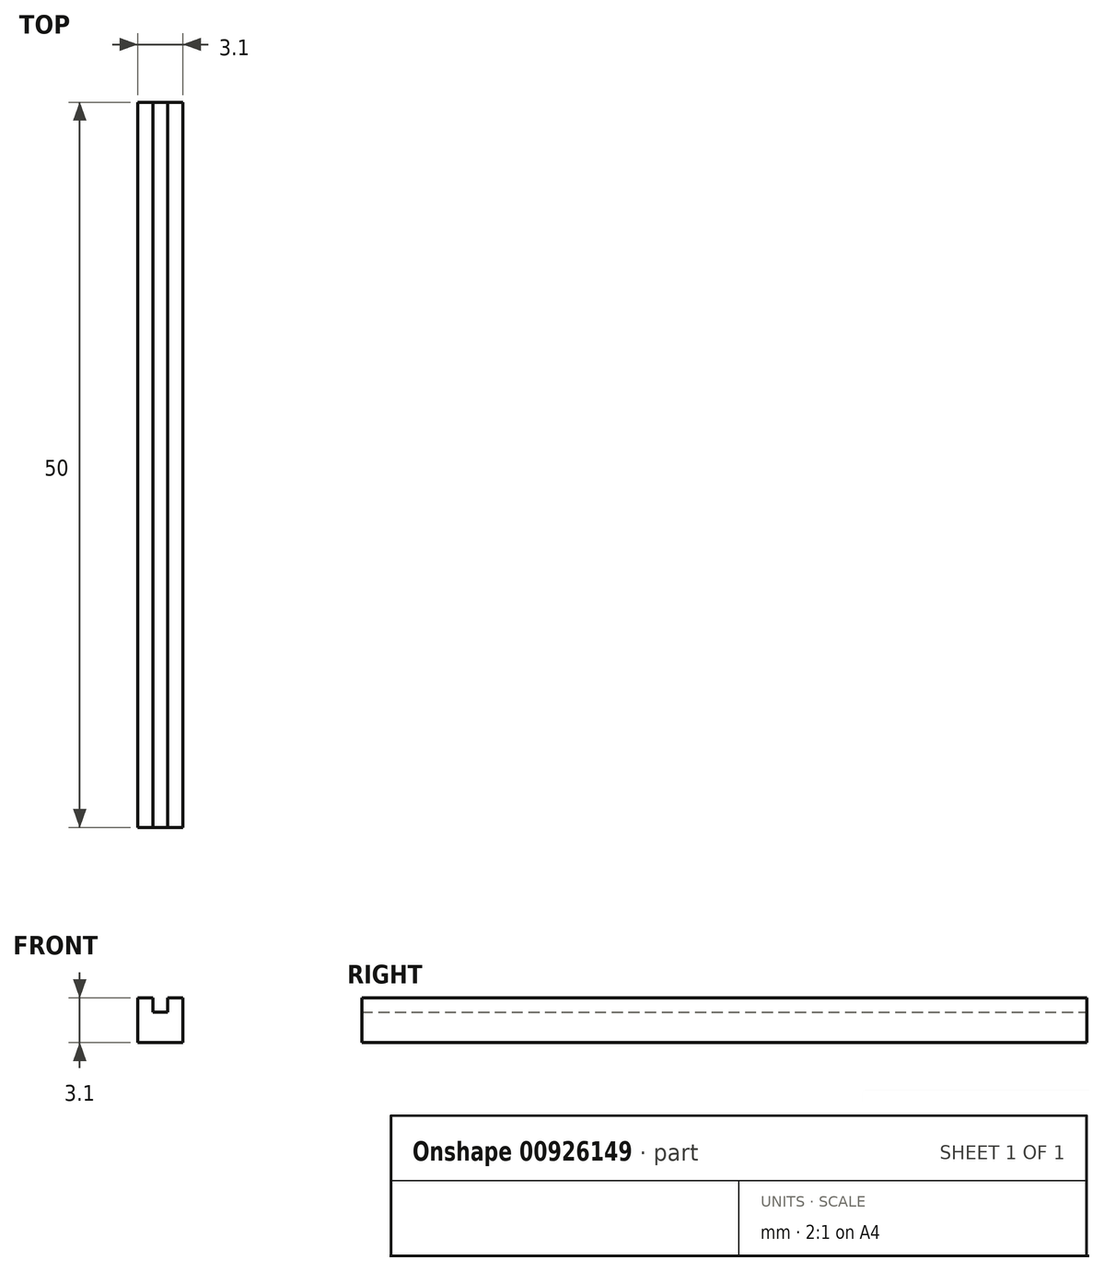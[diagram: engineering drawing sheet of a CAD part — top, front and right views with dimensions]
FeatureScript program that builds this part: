
annotation { "Feature Type Name" : "Feature", "Feature Type Description" : "" }
export const myFeature = defineFeature(function(context is Context, id is Id, definition is map)
    precondition{}
    {
        {
            var Q0;
            Q0=qCreatedBy(makeId("Front.planeOp"),FACE);
            var sketch = newSketch(context, id + "F0", { "sketchPlane" : qUnion([Q0])});
            skLineSegment(sketch, "E0.bottom", {"start": v(0, 0) * mm, "end": v(3.1, 0) * mm});
            skLineSegment(sketch, "E0.top", {"start": v(0, 3.1) * mm, "end": v(3.1, 3.1) * mm});
            skLineSegment(sketch, "E0.left", {"start": v(0, 0) * mm, "end": v(0, 3.1) * mm});
            skLineSegment(sketch, "E0.right", {"start": v(3.1, 0) * mm, "end": v(3.1, 3.1) * mm});
            skLineSegment(sketch, "E1", {"start": v(1.05, 3.1) * mm, "end": v(1.05, 2.1) * mm});
            skLineSegment(sketch, "E2", {"start": v(1.05, 2.1) * mm, "end": v(2.05, 2.1) * mm});
            skLineSegment(sketch, "E3", {"start": v(2.05, 2.1) * mm, "end": v(2.05, 3.1) * mm});
            skSolve(sketch);
        }
        {
            var Q0;
            Q0=makeQuery(id+"F0.imprint","IMPRINT",FACE,{"disambiguationData":[TD([[makeQuery(id+"F0.imprint","IMPRINT",EDGE,{"derivedFrom":sQuery(id+"F0.wireOp",EDGE,"E0.bottom")}),1.0]])]});
            extrude(context, id + "F1", {"entities" : qUnion([Q0]), "depth" : 50 * mm, "offsetDistance" : 25 * mm});
        }
    });
